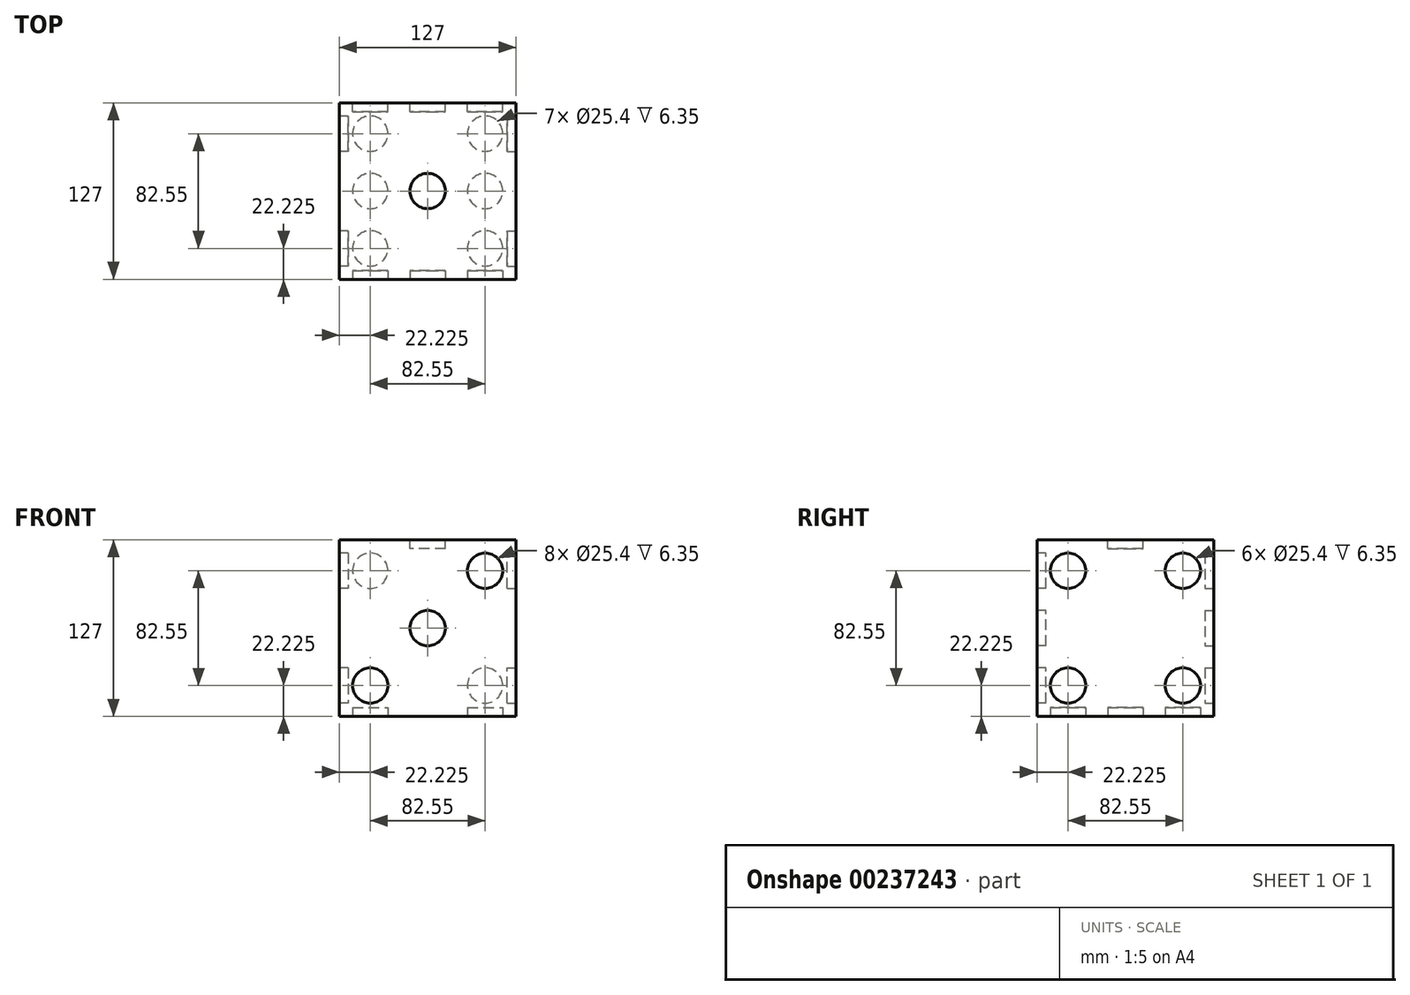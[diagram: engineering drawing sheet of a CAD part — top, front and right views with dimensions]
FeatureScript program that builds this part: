
annotation { "Feature Type Name" : "Feature", "Feature Type Description" : "" }
export const myFeature = defineFeature(function(context is Context, id is Id, definition is map)
    precondition{}
    {
        {
            var Q0;
            Q0=qCreatedBy(makeId("Top.planeOp"),FACE);
            var sketch = newSketch(context, id + "F0", { "sketchPlane" : qUnion([Q0])});
            skLineSegment(sketch, "E0.bottom", {"start": v(0, 0) * mm, "end": v(127, 0) * mm});
            skLineSegment(sketch, "E0.top", {"start": v(0, 127) * mm, "end": v(127, 127) * mm});
            skLineSegment(sketch, "E0.left", {"start": v(0, 0) * mm, "end": v(0, 127) * mm});
            skLineSegment(sketch, "E0.right", {"start": v(127, 0) * mm, "end": v(127, 127) * mm});
            skSolve(sketch);
        }
        {
            var Q0;
            Q0=makeQuery(id+"F0.imprint","IMPRINT",FACE,{"disambiguationData":[TD([[makeQuery(id+"F0.imprint","IMPRINT",EDGE,{"derivedFrom":sQuery(id+"F0.wireOp",EDGE,"E0.bottom")}),1.0]])]});
            extrude(context, id + "F1", {"entities" : qUnion([Q0]), "depth" : 127 * mm});
        }
        {
            var Q0;
            Q0=makeQuery(id+"F1.opExtrude","CAP_FACE",FACE,{"disambiguationData":[OSD([sQuery(id+"F0.wireOp",EDGE,"E0.bottom"),sQuery(id+"F0.wireOp",EDGE,"E0.top"),sQuery(id+"F0.wireOp",EDGE,"E0.left"),sQuery(id+"F0.wireOp",EDGE,"E0.right")])],"isStart":false});
            var sketch = newSketch(context, id + "F2", { "sketchPlane" : qUnion([Q0])});
            skCircle(sketch, "E1", {"center": v(63.5, 63.5) * mm, "radius": 12.7 * mm});
            skSolve(sketch);
        }
        {
            var Q0;
            Q0=makeQuery(id+"F2.imprint","IMPRINT",FACE,{"disambiguationData":[TD([[makeQuery(id+"F2.imprint","IMPRINT",EDGE,{"derivedFrom":sQuery(id+"F2.wireOp",EDGE,"E1")}),1.0]])]});
            var Q1;
            Q1 = qSketchRegion(id + "F1BYeTNI4koWveb_1", true);
            extrude(context, id + "F3", {"entities" : qUnion([Q0, Q1]), "operationType" : NewBodyOperationType.REMOVE, "oppositeDirection" : true, "depth" : 6.35 * mm});
        }
        {
            var Q0;
            Q0=makeQuery(id+"F1.opExtrude","SWEPT_FACE",FACE,{"disambiguationData":[OSD([sQuery(id+"F0.wireOp",EDGE,"E0.left")])]});
            var sketch = newSketch(context, id + "F4", { "sketchPlane" : qUnion([Q0])});
            skCircle(sketch, "E2", {"center": v(-104.78, 22.22) * mm, "radius": 12.7 * mm});
            skCircle(sketch, "E3", {"center": v(-22.23, 104.78) * mm, "radius": 12.7 * mm});
            skSolve(sketch);
        }
        {
            var Q0;
            Q0 = qSketchRegion(id + "F4", true);
            extrude(context, id + "F5", {"entities" : qUnion([Q0]), "operationType" : NewBodyOperationType.REMOVE, "oppositeDirection" : true, "depth" : 6.35 * mm});
        }
        {
            var Q0;
            Q0=makeQuery(id+"F1.opExtrude","SWEPT_FACE",FACE,{"disambiguationData":[OSD([sQuery(id+"F0.wireOp",EDGE,"E0.bottom")])]});
            var sketch = newSketch(context, id + "F6", { "sketchPlane" : qUnion([Q0])});
            skLineSegment(sketch, "E4", {"start": v(0, 0) * mm, "end": v(127, 127) * mm, "construction": true});
            skCircle(sketch, "E5", {"center": v(22.23, 22.23) * mm, "radius": 12.7 * mm});
            skCircle(sketch, "E6", {"center": v(63.5, 63.5) * mm, "radius": 12.7 * mm});
            skCircle(sketch, "E7", {"center": v(104.78, 104.78) * mm, "radius": 12.7 * mm});
            skSolve(sketch);
        }
        {
            var Q0;
            Q0 = qSketchRegion(id + "F6", true);
            extrude(context, id + "F7", {"entities" : qUnion([Q0]), "operationType" : NewBodyOperationType.REMOVE, "oppositeDirection" : true, "depth" : 6.35 * mm});
        }
        {
            var Q0;
            Q0=makeQuery(id+"F1.opExtrude","SWEPT_FACE",FACE,{"disambiguationData":[OSD([sQuery(id+"F0.wireOp",EDGE,"E0.right")])]});
            var sketch = newSketch(context, id + "F8", { "sketchPlane" : qUnion([Q0])});
            skCircle(sketch, "E8", {"center": v(22.22, 22.22) * mm, "radius": 12.7 * mm});
            skCircle(sketch, "E9", {"center": v(22.22, 104.78) * mm, "radius": 12.7 * mm});
            skCircle(sketch, "E10", {"center": v(104.77, 104.78) * mm, "radius": 12.7 * mm});
            skCircle(sketch, "E11", {"center": v(104.77, 22.22) * mm, "radius": 12.7 * mm});
            skSolve(sketch);
        }
        {
            var Q0;
            Q0 = qSketchRegion(id + "F8", true);
            extrude(context, id + "F9", {"entities" : qUnion([Q0]), "operationType" : NewBodyOperationType.REMOVE, "oppositeDirection" : true, "depth" : 6.35 * mm});
        }
        {
            var Q0;
            Q0=makeQuery(id+"F1.opExtrude","SWEPT_FACE",FACE,{"disambiguationData":[OSD([sQuery(id+"F0.wireOp",EDGE,"E0.top")])]});
            var sketch = newSketch(context, id + "F10", { "sketchPlane" : qUnion([Q0])});
            skCircle(sketch, "E12", {"center": v(-22.23, 22.22) * mm, "radius": 12.7 * mm});
            skCircle(sketch, "E13", {"center": v(-104.77, 22.22) * mm, "radius": 12.7 * mm});
            skCircle(sketch, "E14", {"center": v(-104.77, 104.78) * mm, "radius": 12.7 * mm});
            skCircle(sketch, "E15", {"center": v(-22.23, 104.78) * mm, "radius": 12.7 * mm});
            skLineSegment(sketch, "E16", {"start": v(-127, 0) * mm, "end": v(0, 127) * mm, "construction": true});
            skCircle(sketch, "E17", {"center": v(-63.5, 63.5) * mm, "radius": 12.7 * mm});
            skSolve(sketch);
        }
        {
            var Q0;
            Q0 = qSketchRegion(id + "F10", true);
            extrude(context, id + "F11", {"entities" : qUnion([Q0]), "operationType" : NewBodyOperationType.REMOVE, "oppositeDirection" : true, "depth" : 6.35 * mm});
        }
        {
            var Q0;
            Q0=makeQuery(id+"F1.opExtrude","CAP_FACE",FACE,{"disambiguationData":[OSD([sQuery(id+"F0.wireOp",EDGE,"E0.bottom"),sQuery(id+"F0.wireOp",EDGE,"E0.top"),sQuery(id+"F0.wireOp",EDGE,"E0.left"),sQuery(id+"F0.wireOp",EDGE,"E0.right")])],"isStart":true});
            var sketch = newSketch(context, id + "F12", { "sketchPlane" : qUnion([Q0])});
            skCircle(sketch, "E18", {"center": v(22.23, -104.77) * mm, "radius": 12.7 * mm});
            skCircle(sketch, "E19", {"center": v(104.78, -22.23) * mm, "radius": 12.7 * mm});
            skCircle(sketch, "E20", {"center": v(22.23, -63.5) * mm, "radius": 12.7 * mm});
            skCircle(sketch, "E21", {"center": v(104.77, -63.5) * mm, "radius": 12.7 * mm});
            skCircle(sketch, "E22", {"center": v(104.77, -104.78) * mm, "radius": 12.7 * mm});
            skCircle(sketch, "E23", {"center": v(22.23, -22.23) * mm, "radius": 12.7 * mm});
            skSolve(sketch);
        }
        {
            var Q0;
            Q0 = qSketchRegion(id + "F12", true);
            extrude(context, id + "F13", {"entities" : qUnion([Q0]), "operationType" : NewBodyOperationType.REMOVE, "oppositeDirection" : true, "depth" : 6.35 * mm});
        }
    });
